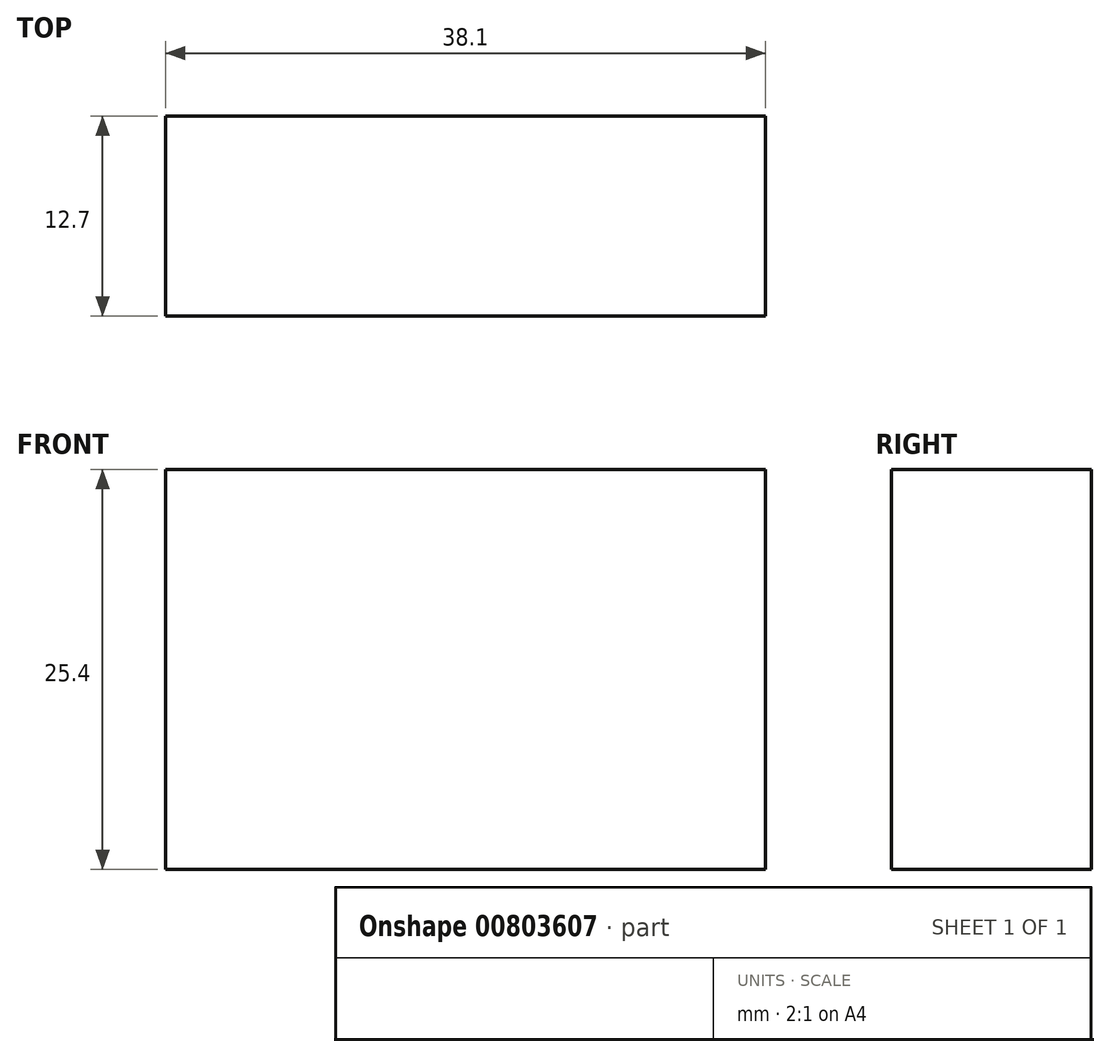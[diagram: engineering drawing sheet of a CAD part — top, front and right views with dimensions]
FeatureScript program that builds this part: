
annotation { "Feature Type Name" : "Feature", "Feature Type Description" : "" }
export const myFeature = defineFeature(function(context is Context, id is Id, definition is map)
    precondition{}
    {
        {
            var Q0;
            Q0=qCreatedBy(makeId("Top.planeOp"),FACE);
            var sketch = newSketch(context, id + "F0", { "sketchPlane" : qUnion([Q0])});
            skLineSegment(sketch, "E0", {"start": v(0, 0) * mm, "end": v(38.1, 0) * mm});
            skLineSegment(sketch, "E1", {"start": v(0, 0) * mm, "end": v(0, -12.7) * mm});
            skLineSegment(sketch, "E2", {"start": v(0, -12.7) * mm, "end": v(38.1, -12.7) * mm});
            skLineSegment(sketch, "E3", {"start": v(38.1, 0) * mm, "end": v(38.1, -12.7) * mm});
            skSolve(sketch);
        }
        {
            var Q0;
            Q0=makeQuery(id+"F0.imprint","IMPRINT",FACE,{"disambiguationData":[TD([[makeQuery(id+"F0.imprint","IMPRINT",EDGE,{"derivedFrom":sQuery(id+"F0.wireOp",EDGE,"E0")}),-1.0]])]});
            extrude(context, id + "F1", {"entities" : qUnion([Q0]), "depth" : 25.4 * mm, "offsetDistance" : 25.4 * mm});
        }
    });
